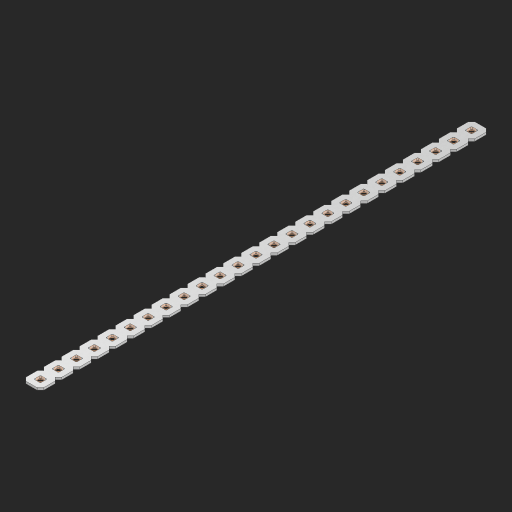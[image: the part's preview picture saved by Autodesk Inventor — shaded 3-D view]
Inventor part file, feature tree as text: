
AUTODESK INVENTOR PART (.ipt)
format: ipt  version: 2023 (Build 270158000, 158)  size: 548,864 bytes
history: native  units: in
note: dims shown in document units (in); Inventor stores cm internally (conversion verified against a paired STEP export)
features: other x26, extrude x24, sketch x2, pattern_linear x1
ambient origin geometry x8: Origin, YZ Plane, XZ Plane, XY Plane, X Axis, Y Axis, Z Axis, Center Point
bodies: Solid1 (feature_tree), Body (feature_tree)
feature tree (53):
  pattern_linear  "Rectangular Pattern1"  Spacing1=0.09in  [1 undecoded]
  sketch  "Sketch1"  dims[d1=0.5in]
  sketch  "Sketch2"  dims[d2=0.182in d3=0.09in d4=0.09in d5=0.09in d6=0.09in d7=0.09in d8=0.09in d9=0.09in d10=0.09in d11=0.02in d13=0.0in d14=0.172in d15=0.0625in d16=0.0in d19=0.5in d22=0.5in]
  other  "Srf1"
  other  "Srf126"
  other  "Srf127"
  other  "Srf128"
  other  "Srf129"
  other  "Srf130"
  other  "Srf131"
  other  "Srf250"
  other  "Srf251"
  other  "Srf252"
  other  "Srf253"
  other  "Srf254"
  other  "Srf255"
  other  "Srf256"
  other  "Srf257"
  other  "Srf258"
  other  "Srf259"
  other  "Srf260"
  other  "Srf261"
  other  "Srf262"
  other  "Srf263"
  other  "Srf264"
  other  "Srf265"
  other  "Srf266"
  other  "Srf267"
  other  "Circle"
  extrude  "ExtrusionSrf126"  Depth=0.09in
  extrude  "ExtrusionSrf127"  Depth=0.09in
  extrude  "ExtrusionSrf128"  Depth=0.09in
  extrude  "ExtrusionSrf129"  Depth=0.09in
  extrude  "ExtrusionSrf130"  Depth=0.09in
  extrude  "ExtrusionSrf131"  Depth=0.09in
  extrude  "ExtrusionSrf250"  Depth=0.09in
  extrude  "ExtrusionSrf251"  Depth=0.02in
  extrude  "ExtrusionSrf252"  TaperAngle=0.0deg  [1 undecoded]
  extrude  "ExtrusionSrf253"  Depth=0.5in
  extrude  "ExtrusionSrf254"  Depth=0.0625in TaperAngle=0.0deg
  extrude  "ExtrusionSrf255"  Depth=0.5in
  extrude  "ExtrusionSrf256"  Depth=0.5in
  extrude  "ExtrusionSrf257"  [1 undecoded]
  extrude  "ExtrusionSrf258"  [1 undecoded]
  extrude  "ExtrusionSrf259"  [1 undecoded]
  extrude  "ExtrusionSrf260"  [1 undecoded]
  extrude  "ExtrusionSrf261"  [1 undecoded]
  extrude  "ExtrusionSrf262"  [1 undecoded]
  extrude  "ExtrusionSrf263"  [1 undecoded]
  extrude  "ExtrusionSrf264"  [1 undecoded]
  extrude  "ExtrusionSrf265"  [1 undecoded]
  extrude  "ExtrusionSrf266"  [1 undecoded]
  extrude  "ExtrusionSrf267"  [1 undecoded]
note: 13 required parameter values undecoded (feature->parameter linkage not recoverable at this tier; creation-order binding heuristic only, values carry confidence <= 0.55)
